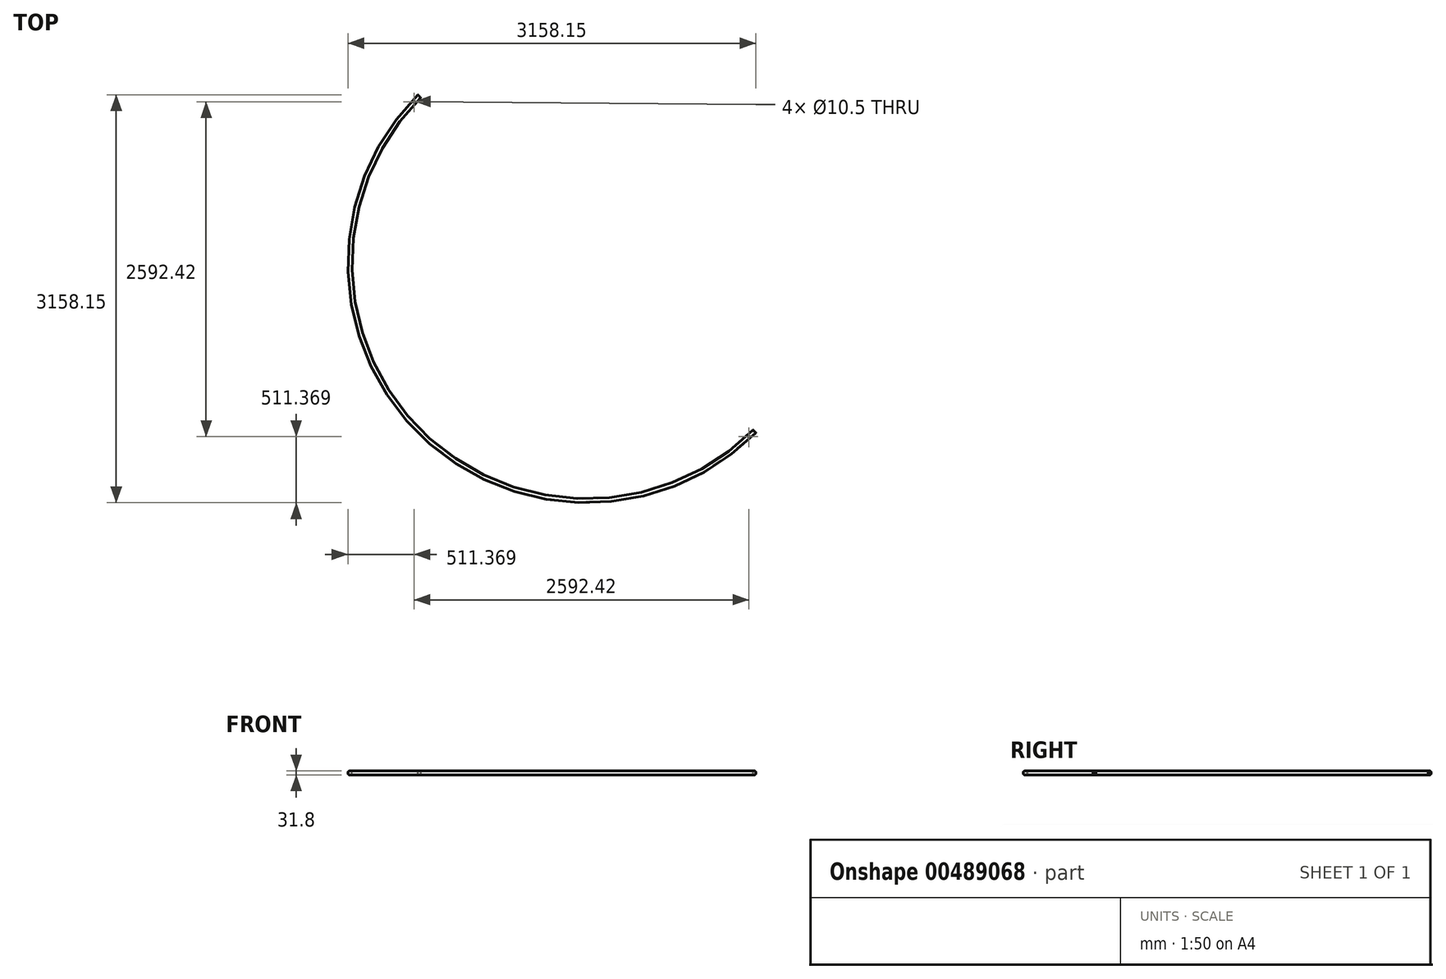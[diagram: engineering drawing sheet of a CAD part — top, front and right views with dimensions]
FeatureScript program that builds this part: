
annotation { "Feature Type Name" : "Feature", "Feature Type Description" : "" }
export const myFeature = defineFeature(function(context is Context, id is Id, definition is map)
    precondition{}
    {
        {
            var Q0;
            Q0=qCreatedBy(makeId("Right.planeOp"),FACE);
            var sketch = newSketch(context, id + "F0", { "sketchPlane" : qUnion([Q0])});
            skCircle(sketch, "E0", {"center": v(1834.1, 0) * mm, "radius": 15.9 * mm});
            skCircle(sketch, "E1.0", {"center": v(1834.1, 0) * mm, "radius": 12.7 * mm});
            skLineSegment(sketch, "E2", {"start": v(0, 0) * mm, "end": v(0, 147.15) * mm, "construction": true});
            skSolve(sketch);
        }
        {
            var Q0;
            Q0 = qSketchRegion(id + "F0", true);
            var Q1;
            Q1=sQuery(id+"F0.wireOp",EDGE,"E2");
            revolve(context, id + "F1", {"entities" : qUnion([Q0]), "axis" : qUnion([Q1]), "revolveType" : RevolveType.FULL});
        }
        {
            var Q0;
            Q0=qCreatedBy(makeId("Top.planeOp"),FACE);
            var sketch = newSketch(context, id + "F2", { "sketchPlane" : qUnion([Q0])});
            skCircle(sketch, "E3", {"center": v(0, 1835) * mm, "radius": 6.25 * mm});
            skSolve(sketch);
        }
        {
            var Q0;
            Q0 = qSketchRegion(id + "F2", true);
            extrude(context, id + "F3", {"entities" : qUnion([Q0]), "operationType" : NewBodyOperationType.REMOVE, "endBound" : BoundingType.THROUGH_ALL, "oppositeDirection" : true, "depth" : 25 * mm, "hasSecondDirection" : true, "secondDirectionBound" : BoundingType.THROUGH_ALL, "secondDirectionOppositeDirection" : false, "secondDirectionDepth" : 25 * mm});
        }
        {
            var Q0;
            Q0=qCreatedBy(makeId("Top.planeOp"),FACE);
            var sketch = newSketch(context, id + "F4", { "sketchPlane" : qUnion([Q0])});
            skLineSegment(sketch, "E4", {"start": v(0, 0) * mm, "end": v(1308.15, -1308.15) * mm});
            skLineSegment(sketch, "E5", {"start": v(0, 0) * mm, "end": v(0, 1280.24) * mm, "construction": true});
            skLineSegment(sketch, "E6", {"start": v(0, 0) * mm, "end": v(-1308.15, 1308.15) * mm});
            skArc(sketch, "E7", {"start": v(1308.15, -1308.15) * mm, "mid": v(1308.15, 1308.15) * mm, "end": v(-1308.15, 1308.15) * mm});
            skSolve(sketch);
        }
        {
            var Q0;
            Q0 = qSketchRegion(id + "F4", true);
            extrude(context, id + "F5", {"entities" : qUnion([Q0]), "operationType" : NewBodyOperationType.REMOVE, "endBound" : BoundingType.THROUGH_ALL, "oppositeDirection" : true, "depth" : 25 * mm, "hasSecondDirection" : true, "secondDirectionBound" : BoundingType.THROUGH_ALL, "secondDirectionOppositeDirection" : false, "secondDirectionDepth" : 25 * mm});
        }
        {
            var Q0;
            Q0=qCreatedBy(makeId("Top.planeOp"),FACE);
            var sketch = newSketch(context, id + "F6", { "sketchPlane" : qUnion([Q0])});
            skArc(sketch, "E8", {"start": v(1296.9, -1296.9) * mm, "mid": v(1275.52, -1317.94) * mm, "end": v(1253.79, -1338.63) * mm, "construction": true});
            skCircle(sketch, "E9", {"center": v(1253.79, -1338.63) * mm, "radius": 5.25 * mm});
            skLineSegment(sketch, "E10", {"start": v(0, 0) * mm, "end": v(-1018.16, -1018.16) * mm, "construction": true});
            skCircle(sketch, "E11.MirrorC", {"center": v(-1338.63, 1253.79) * mm, "radius": 5.25 * mm});
            skSolve(sketch);
        }
        {
            var Q0;
            Q0 = qSketchRegion(id + "F6", true);
            extrude(context, id + "F7", {"entities" : qUnion([Q0]), "operationType" : NewBodyOperationType.REMOVE, "endBound" : BoundingType.THROUGH_ALL, "oppositeDirection" : true, "depth" : 25 * mm, "hasSecondDirection" : true, "secondDirectionBound" : BoundingType.THROUGH_ALL, "secondDirectionOppositeDirection" : false, "secondDirectionDepth" : 25 * mm});
        }
    });
